# Revit family: Legrand Linkeo coffrets pivotants avec panneaux latéraux amovibles
name_source: partatom
category: Equipement spécialisé
units: mm (PartAtom-declared; Revit-internal decimal feet)

## family parameters
Basée sur le plan de construction = Non
Cote de connecteur circulaire = Utiliser le diamètre
Couper avec des vides une fois chargée = Non
Numéro OmniClass = 23.80.30.11.17
Partagée = Oui
Point de calcul de pièce = Non
Titre OmniClass = Distribution Boards and Control Panels
Toujours verticalement = Oui
Type d'élément = Normal

## types (5) — shared parameters
Avec mise à la terre = Oui
Avec parois latérales = Oui
Avec porte frontale = Oui
Avec tôle de toit = Oui
Classe d'application = Coffrets Legrand
Couleur = gris
Dimension modulaire = 482.6 mm (19 pouces)
Démontable = Oui
Emplacement de rack = 40 mm  [stored 0.131234 ft]
Epaisseur (mm) = 1.5 mm  [stored 0.00492126 ft]
Fabricant = Legrand
Finition de surface = Poudré
Finition du rail profilé = En forme de L
Fonction = Coffrets pivotants Legrand Linkeo
Indice de protection IK = IK08
Indice de protection IP = IP20
Largeur (mm) = 642 mm  [stored 2.1063 ft]
Lien e-catalogue = https://www.legrand.fr
Matériau = Acier
Modèle = Corps pivotant
Nombre de portes = 1
Passage utile en largeur (mm) = 527 mm  [stored 1.729 ft]
Profondeur (mm) = 615 mm  [stored 2.01772 ft]
Profondeur du modèle = 458 mm
RAL = 7016
Type d'aération = Passif
Type de montage = Frontal
zero-valued in all types: Elévation par défaut

## per-type parameters (varying)
| type | Capacité | Capacité de charge max | EAN | Hauteur (mm) | Nombre d'unités en hauteur | Passage utile en hauteur (mm) | Référence Legrand |
| Coffret pivotant Legrand Linkeo 9U W600 D610 646221.rfa | 9 | 27 | 3414970967893 | 492 mm  [stored 1.61417 ft] | 9 | 422 mm  [stored 1.38451 ft] | 646221 |
| Coffret pivotant Legrand Linkeo 12U W600 D610 646222.rfa | 12 | 36 | 3414970967909 | 625 mm  [stored 2.05052 ft] | 12 | 555 mm  [stored 1.82087 ft] | 646222 |
| Coffret pivotant Legrand Linkeo 15U W600 D610 646223.rfa | 15 | 45 | 3414970967916 | 759 mm  [stored 2.49016 ft] | 15 | 688 mm  [stored 2.25722 ft] | 646223 |
| Coffret pivotant Legrand Linkeo 18U W600 D610 646224.rfa | 18 | 54 | 3414970967923 | 892 mm  [stored 2.92651 ft] | 18 | 821 mm  [stored 2.69357 ft] | 646224 |
| Coffret pivotant Legrand Linkeo 21U W600 D610 646225.rfa | 21 | 63 | 3414970967930 | 1025 mm  [stored 3.36286 ft] | 21 | 955 mm  [stored 3.1332 ft] | 646225 |

note: column(s) folded — value = type name in every type: Libellé BIM

note: [stored X ft] marks values corroborated as IEEE doubles in the binary element streams (Revit-internal decimal feet)
